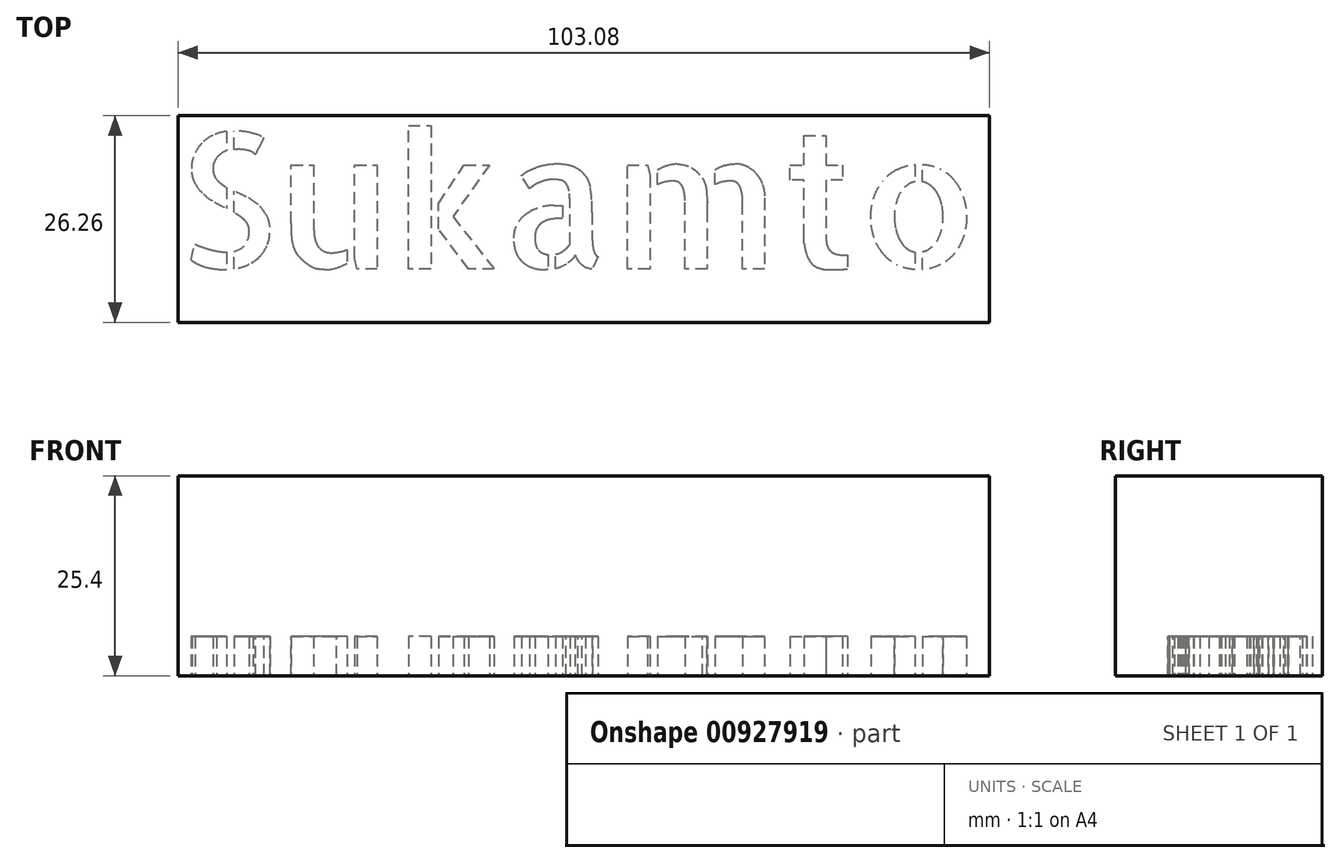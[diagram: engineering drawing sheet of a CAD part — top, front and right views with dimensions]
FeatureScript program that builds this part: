
annotation { "Feature Type Name" : "Feature", "Feature Type Description" : "" }
export const myFeature = defineFeature(function(context is Context, id is Id, definition is map)
    precondition{}
    {
        {
            var Q0;
            Q0=qCreatedBy(makeId("Top.planeOp"),FACE);
            var sketch = newSketch(context, id + "F0", { "sketchPlane" : qUnion([Q0])});
            skText(sketch, "E0", { "text": "Sukamto", "fontName": "AllertaStencil-Regular.ttf"});
            const initialGuessF0  = {"E0": [-0.03511, 0.02757, 1, 0, 0.01726]};
            skSetInitialGuess(sketch, initialGuessF0);
            skSolve(sketch);
        }
        {
            var Q0;
            Q0=qCreatedBy(makeId("Top.planeOp"),FACE);
            var sketch = newSketch(context, id + "F1", { "sketchPlane" : qUnion([Q0])});
            skLineSegment(sketch, "E1.bottom", {"start": v(-34.86, 20.77) * mm, "end": v(68.22, 20.77) * mm});
            skLineSegment(sketch, "E1.top", {"start": v(-34.86, 47.03) * mm, "end": v(68.22, 47.03) * mm});
            skLineSegment(sketch, "E1.left", {"start": v(-34.86, 20.77) * mm, "end": v(-34.86, 47.03) * mm});
            skLineSegment(sketch, "E1.right", {"start": v(68.22, 20.77) * mm, "end": v(68.22, 47.03) * mm});
            skSolve(sketch);
        }
        {
            var Q0;
            Q0 = qSketchRegion(id + "F0", true);
            extrude(context, id + "F2", {"entities" : qUnion([Q0]), "depth" : 5 * mm, "offsetDistance" : 25.4 * mm});
        }
        {
            var Q0;
            Q0=makeQuery(id+"F1.imprint","IMPRINT",FACE,{"disambiguationData":[TD([[makeQuery(id+"F1.imprint","IMPRINT",EDGE,{"derivedFrom":sQuery(id+"F1.wireOp",EDGE,"E1.bottom")}),1.0]])]});
            extrude(context, id + "F3", {"entities" : qUnion([Q0]), "depth" : 25.4 * mm, "offsetDistance" : 25.4 * mm});
        }
    });
